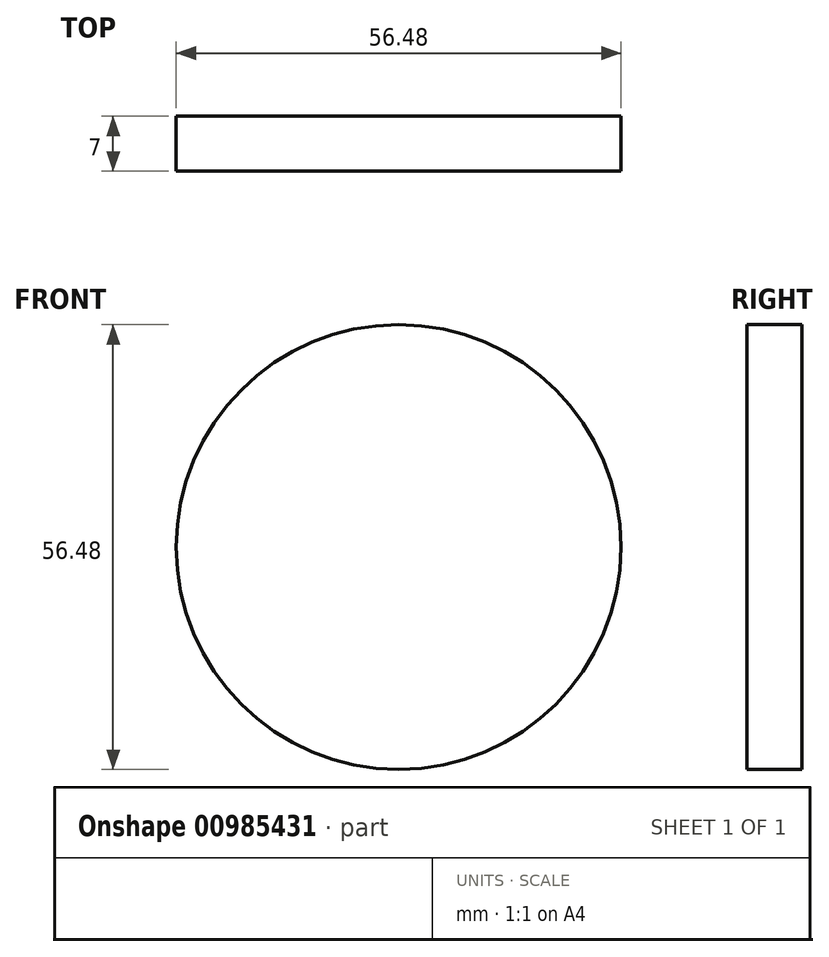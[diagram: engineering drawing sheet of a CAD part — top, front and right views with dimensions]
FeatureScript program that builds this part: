
annotation { "Feature Type Name" : "Feature", "Feature Type Description" : "" }
export const myFeature = defineFeature(function(context is Context, id is Id, definition is map)
    precondition{}
    {
        {
            var Q0;
            Q0=qCreatedBy(makeId("Front.planeOp"),FACE);
            var sketch = newSketch(context, id + "F0", { "sketchPlane" : qUnion([Q0])});
            skCircle(sketch, "E0", {"center": v(0, 0) * mm, "radius": 28.24 * mm});
            skSolve(sketch);
        }
        {
            var Q0;
            Q0 = qSketchRegion(id + "F0", true);
            extrude(context, id + "F1", {"entities" : qUnion([Q0]), "depth" : 7 * mm, "offsetDistance" : 25 * mm});
        }
    });
